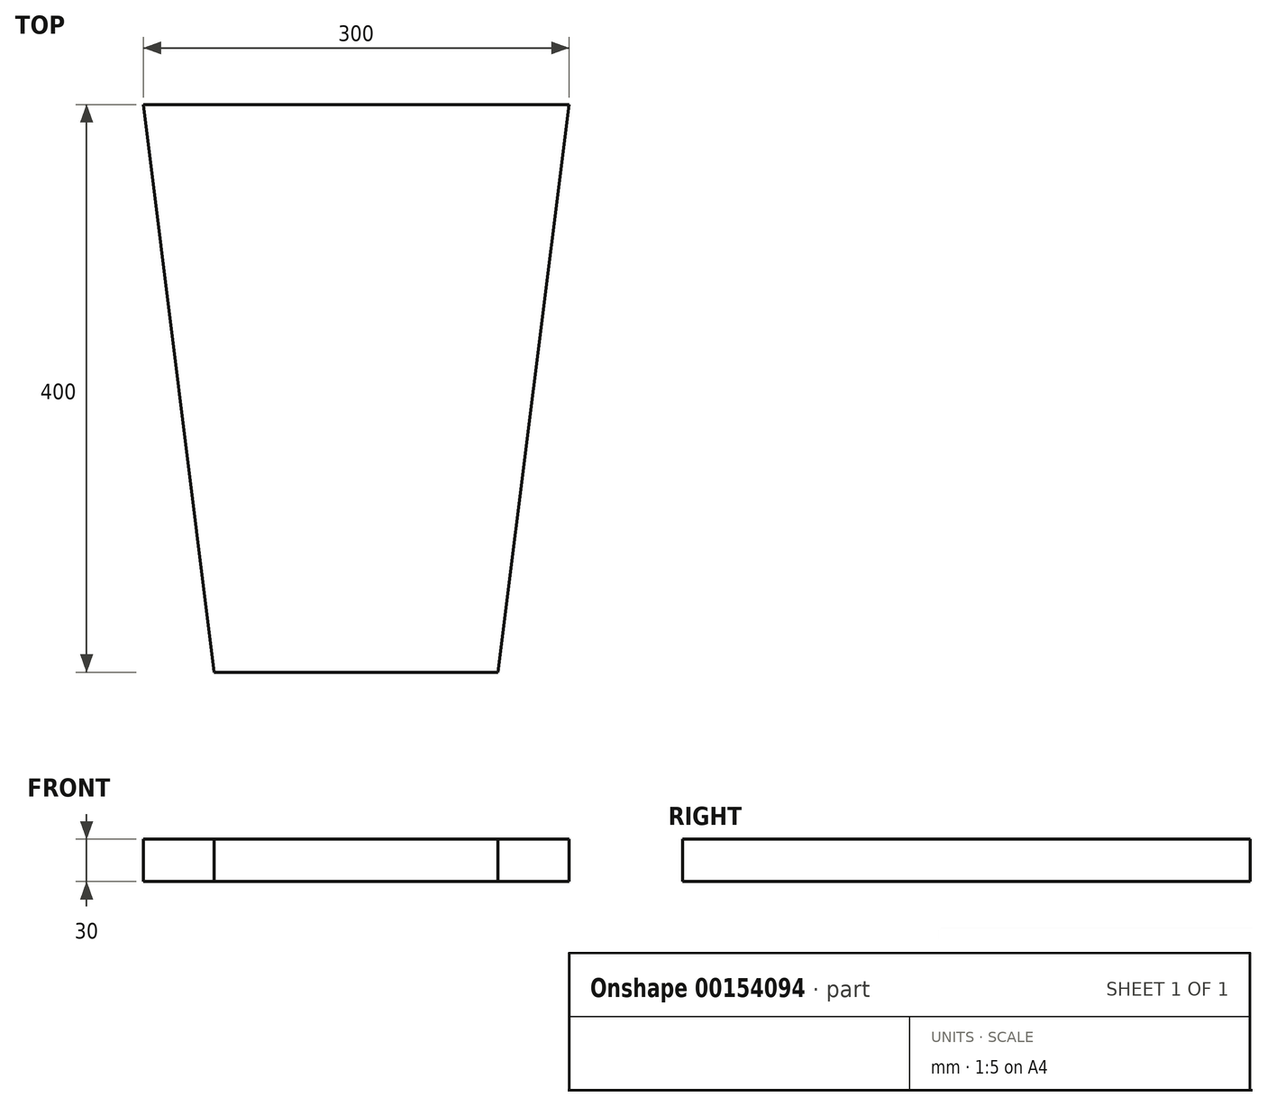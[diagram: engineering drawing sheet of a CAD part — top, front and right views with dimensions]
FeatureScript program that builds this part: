
annotation { "Feature Type Name" : "Feature", "Feature Type Description" : "" }
export const myFeature = defineFeature(function(context is Context, id is Id, definition is map)
    precondition{}
    {
        {
            var Q0;
            Q0=qCreatedBy(makeId("Top.planeOp"),FACE);
            var sketch = newSketch(context, id + "F0", { "sketchPlane" : qUnion([Q0])});
            skLineSegment(sketch, "E0", {"start": v(0, 200) * mm, "end": v(-150, 200) * mm});
            skLineSegment(sketch, "E1", {"start": v(-150, 200) * mm, "end": v(-100, -200) * mm});
            skLineSegment(sketch, "E2", {"start": v(-100, -200) * mm, "end": v(0, -200) * mm});
            skLineSegment(sketch, "E3.MirrorCS", {"start": v(0, 200) * mm, "end": v(150, 200) * mm});
            skLineSegment(sketch, "E4.MirrorCS", {"start": v(150, 200) * mm, "end": v(100, -200) * mm});
            skLineSegment(sketch, "E5.MirrorCS", {"start": v(100, -200) * mm, "end": v(0, -200) * mm});
            skSolve(sketch);
        }
        {
            var Q0;
            Q0=makeQuery(id+"F0.imprint","IMPRINT",FACE,{"disambiguationData":[TD([[makeQuery(id+"F0.imprint","IMPRINT",EDGE,{"derivedFrom":sQuery(id+"F0.wireOp",EDGE,"E0")}),1.0]])]});
            extrude(context, id + "F1", {"entities" : qUnion([Q0]), "depth" : 30 * mm});
        }
    });
